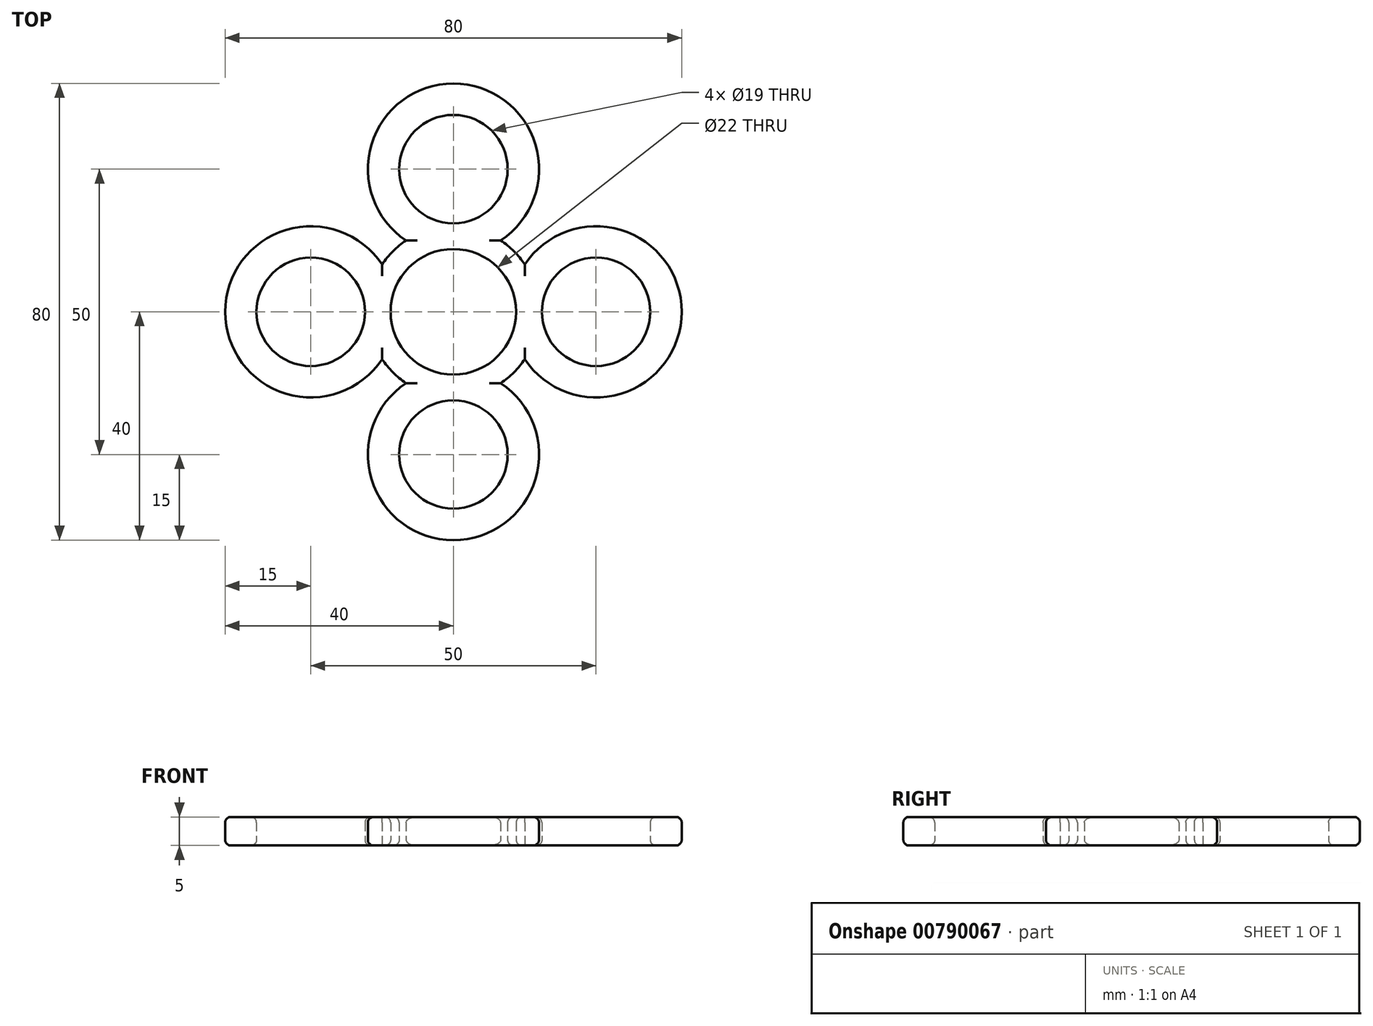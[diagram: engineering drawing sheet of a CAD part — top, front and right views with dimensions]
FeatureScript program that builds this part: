
annotation { "Feature Type Name" : "Feature", "Feature Type Description" : "" }
export const myFeature = defineFeature(function(context is Context, id is Id, definition is map)
    precondition{}
    {
        {
            var Q0;
            Q0=qCreatedBy(makeId("Top.planeOp"),FACE);
            var sketch = newSketch(context, id + "F0", { "sketchPlane" : qUnion([Q0])});
            skArc(sketch, "E0", {"start": v(0, 11) * mm, "mid": v(-11, 0) * mm, "end": v(0, -11) * mm});
            skArc(sketch, "E1", {"start": v(-12.5, -8.3) * mm, "mid": v(-10.6, -10.6) * mm, "end": v(-8.3, -12.5) * mm});
            skCircle(sketch, "E2", {"center": v(-25, 0) * mm, "radius": 9.5 * mm});
            skArc(sketch, "E3", {"start": v(-12.5, 8.3) * mm, "mid": v(-40, 0) * mm, "end": v(-12.5, -8.3) * mm});
            skLineSegment(sketch, "E4", {"start": v(0, 0) * mm, "end": v(0, 15) * mm});
            skLineSegment(sketch, "E5", {"start": v(0, 11) * mm, "end": v(0, -15) * mm});
            skArc(sketch, "E6.trimOffspring", {"start": v(-8.3, 12.5) * mm, "mid": v(-10.6, 10.6) * mm, "end": v(-12.5, 8.3) * mm});
            skLineSegment(sketch, "E7.MirrorCS", {"start": v(0, 0) * mm, "end": v(0, -11) * mm});
            skArc(sketch, "E8.MirrorCS", {"start": v(0, 11) * mm, "mid": v(11, 0) * mm, "end": v(0, -11) * mm});
            skArc(sketch, "E9.MirrorCS", {"start": v(8.3, 12.5) * mm, "mid": v(10.6, 10.6) * mm, "end": v(12.5, 8.3) * mm});
            skArc(sketch, "E10.MirrorCS", {"start": v(12.5, 8.3) * mm, "mid": v(40, 0) * mm, "end": v(12.5, -8.3) * mm});
            skArc(sketch, "E11.MirrorCS", {"start": v(12.5, -8.3) * mm, "mid": v(10.6, -10.6) * mm, "end": v(8.3, -12.5) * mm});
            skCircle(sketch, "E12.MirrorC", {"center": v(25, 0) * mm, "radius": 9.5 * mm});
            skLineSegment(sketch, "E13", {"start": v(0, 0) * mm, "end": v(0, 15.5) * mm});
            skCircle(sketch, "E14", {"center": v(0, 25) * mm, "radius": 9.5 * mm});
            skArc(sketch, "E15", {"start": v(8.3, 12.5) * mm, "mid": v(0, 40) * mm, "end": v(-8.3, 12.5) * mm});
            skLineSegment(sketch, "E16", {"start": v(0, -10) * mm, "end": v(0, -11) * mm});
            skCircle(sketch, "E17", {"center": v(0, -25) * mm, "radius": 9.5 * mm});
            skArc(sketch, "E18", {"start": v(-8.3, -12.5) * mm, "mid": v(0, -40) * mm, "end": v(8.3, -12.5) * mm});
            skPoint(sketch, "E19.orphan", {"position": v(0, 15) * mm});
            skLineSegment(sketch, "E20.trimOffspring", {"start": v(0, -15) * mm, "end": v(0, -25) * mm});
            skSolve(sketch);
        }
        {
            var Q0;
            Q0 = qSketchRegion(id + "F0", true);
            extrude(context, id + "F1", {"entities" : qUnion([Q0]), "depth" : 5 * mm, "offsetDistance" : 25 * mm});
        }
        {
            var Q0;
            Q0=makeQuery(id+"F1.opExtrude","CAP_FACE",FACE,{"disambiguationData":[OSD([sQuery(id+"F0.wireOp",EDGE,"E0"),sQuery(id+"F0.wireOp",EDGE,"E1"),sQuery(id+"F0.wireOp",EDGE,"E2"),sQuery(id+"F0.wireOp",EDGE,"E3"),sQuery(id+"F0.wireOp",EDGE,"E6.trimOffspring"),sQuery(id+"F0.wireOp",EDGE,"E8.MirrorCS"),sQuery(id+"F0.wireOp",EDGE,"E9.MirrorCS"),sQuery(id+"F0.wireOp",EDGE,"E10.MirrorCS"),sQuery(id+"F0.wireOp",EDGE,"E11.MirrorCS"),sQuery(id+"F0.wireOp",EDGE,"E12.MirrorC")])],"isStart":true});
            var Q1;
            Q1=makeQuery(id+"F1.opExtrude","CAP_FACE",FACE,{"disambiguationData":[OSD([sQuery(id+"F0.wireOp",EDGE,"E0"),sQuery(id+"F0.wireOp",EDGE,"E1"),sQuery(id+"F0.wireOp",EDGE,"E2"),sQuery(id+"F0.wireOp",EDGE,"E3"),sQuery(id+"F0.wireOp",EDGE,"E6.trimOffspring"),sQuery(id+"F0.wireOp",EDGE,"E8.MirrorCS"),sQuery(id+"F0.wireOp",EDGE,"E9.MirrorCS"),sQuery(id+"F0.wireOp",EDGE,"E10.MirrorCS"),sQuery(id+"F0.wireOp",EDGE,"E11.MirrorCS"),sQuery(id+"F0.wireOp",EDGE,"E12.MirrorC")])],"isStart":false});
            fillet(context, id + "F2", {"entities" : qUnion([Q0, Q1]), "radius" : 1 * mm, "tangentPropagation" : true, "allowEdgeOverflow" : false});
        }
    });
